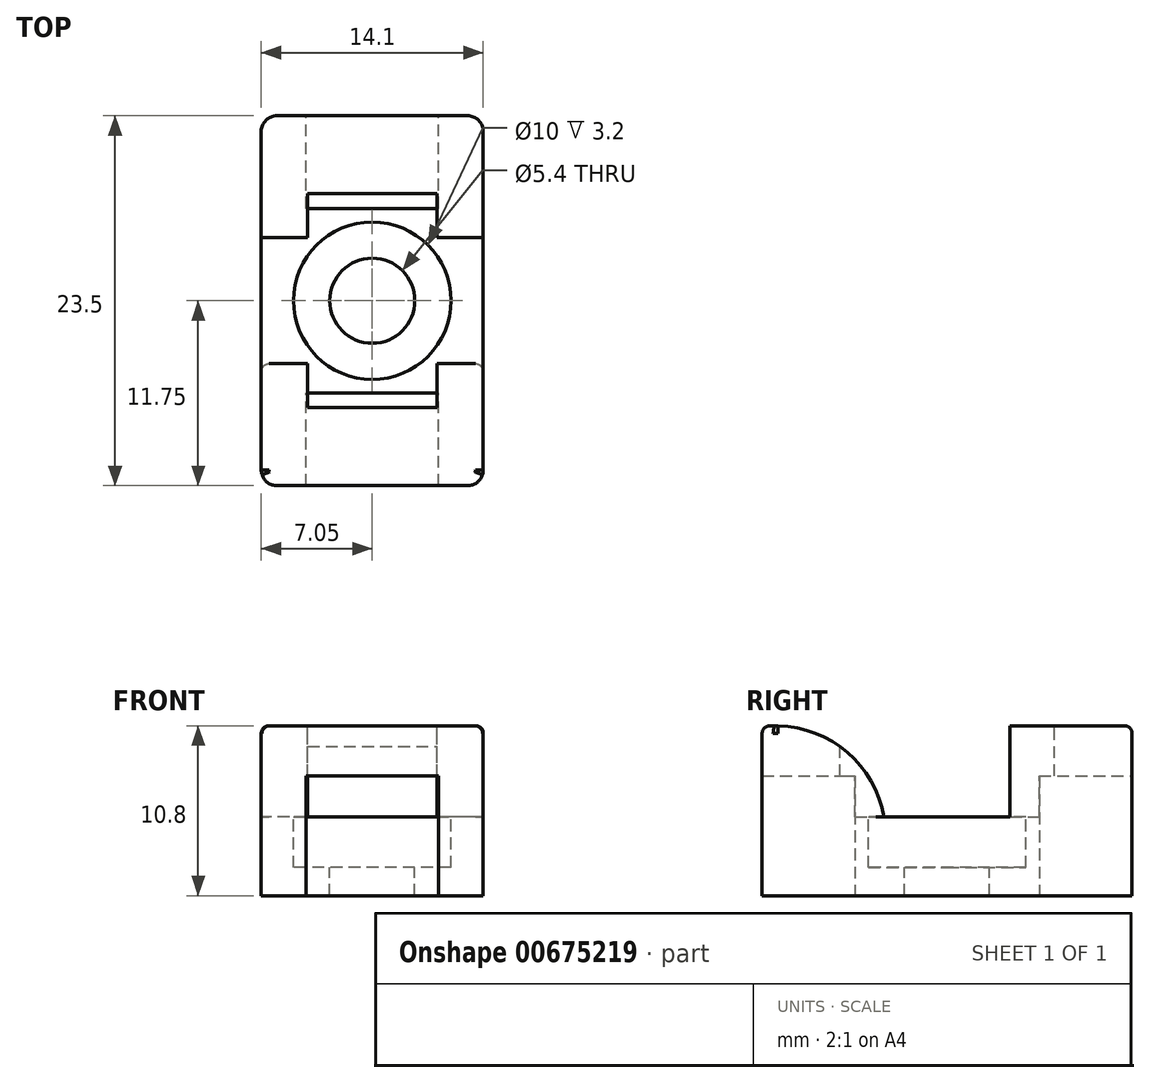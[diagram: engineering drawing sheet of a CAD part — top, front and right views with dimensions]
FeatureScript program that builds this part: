
annotation { "Feature Type Name" : "Feature", "Feature Type Description" : "" }
export const myFeature = defineFeature(function(context is Context, id is Id, definition is map)
    precondition{}
    {
        {
            var Q0;
            Q0=qCreatedBy(makeId("Top.planeOp"),FACE);
            var sketch = newSketch(context, id + "F0", { "sketchPlane" : qUnion([Q0])});
            skLineSegment(sketch, "E0.bottom", {"start": v(7.05, 11.75) * mm, "end": v(-7.05, 11.75) * mm});
            skLineSegment(sketch, "E0.top", {"start": v(7.05, -11.75) * mm, "end": v(-7.05, -11.75) * mm});
            skLineSegment(sketch, "E0.left", {"start": v(7.05, 11.75) * mm, "end": v(7.05, -11.75) * mm});
            skLineSegment(sketch, "E0.right", {"start": v(-7.05, 11.75) * mm, "end": v(-7.05, -11.75) * mm});
            skPoint(sketch, "E0.middle", {"position": v(0, 0) * mm});
            skSolve(sketch);
        }
        {
            var Q0;
            Q0=qSketchRegion(id+"F0",true);
            extrude(context, id + "F1", {"entities" : qUnion([Q0]), "depth" : 10.8 * mm, "offsetDistance" : 25 * mm});
        }
        {
            var Q0;
            Q0=makeQuery(id+"F1.opExtrude","CAP_FACE",FACE,{"disambiguationData":[OSD([sQuery(id+"F0.wireOp",EDGE,"E0.bottom"),sQuery(id+"F0.wireOp",EDGE,"E0.top"),sQuery(id+"F0.wireOp",EDGE,"E0.left"),sQuery(id+"F0.wireOp",EDGE,"E0.right")])],"isStart":false});
            var sketch = newSketch(context, id + "F2", { "sketchPlane" : qUnion([Q0])});
            skLineSegment(sketch, "E1.bottom", {"start": v(4.1, -6.8) * mm, "end": v(-4.1, -6.8) * mm});
            skLineSegment(sketch, "E1.top", {"start": v(4.1, 6.8) * mm, "end": v(-4.1, 6.8) * mm});
            skLineSegment(sketch, "E1.left", {"start": v(4.1, -6.8) * mm, "end": v(4.1, 6.8) * mm});
            skLineSegment(sketch, "E1.right", {"start": v(-4.1, -6.8) * mm, "end": v(-4.1, 6.8) * mm});
            skPoint(sketch, "E1.middle", {"position": v(0, 0) * mm});
            skLineSegment(sketch, "E2.bottom", {"start": v(7.05, -4) * mm, "end": v(-7.05, -4) * mm});
            skLineSegment(sketch, "E2.top", {"start": v(7.05, 4) * mm, "end": v(-7.05, 4) * mm});
            skLineSegment(sketch, "E2.left", {"start": v(7.05, -4) * mm, "end": v(7.05, 4) * mm});
            skLineSegment(sketch, "E2.right", {"start": v(-7.05, -4) * mm, "end": v(-7.05, 4) * mm});
            skSolve(sketch);
        }
        {
            var Q0;
            Q0=qSketchRegion(id+"F2",true);
            extrude(context, id + "F3", {"entities" : qUnion([Q0]), "operationType" : NewBodyOperationType.REMOVE, "oppositeDirection" : true, "depth" : 5.8 * mm, "offsetDistance" : 25 * mm});
        }
        {
            var Q0;
            Q0=makeQuery(id+"F1.opExtrude","CAP_FACE",FACE,{"disambiguationData":[OSD([sQuery(id+"F0.wireOp",EDGE,"E0.bottom"),sQuery(id+"F0.wireOp",EDGE,"E0.top"),sQuery(id+"F0.wireOp",EDGE,"E0.left"),sQuery(id+"F0.wireOp",EDGE,"E0.right")])],"isStart":true});
            var sketch = newSketch(context, id + "F4", { "sketchPlane" : qUnion([Q0])});
            skLineSegment(sketch, "E3.bottom", {"start": v(-4.2, -5.85) * mm, "end": v(4.2, -5.85) * mm});
            skLineSegment(sketch, "E3.top", {"start": v(-4.2, -11.75) * mm, "end": v(4.2, -11.75) * mm});
            skLineSegment(sketch, "E3.left", {"start": v(-4.2, -5.85) * mm, "end": v(-4.2, -11.75) * mm});
            skLineSegment(sketch, "E3.right", {"start": v(4.2, -5.85) * mm, "end": v(4.2, -11.75) * mm});
            skPoint(sketch, "E3.middle", {"position": v(0, -8.8) * mm});
            skLineSegment(sketch, "E4.bottom", {"start": v(-4.2, 11.75) * mm, "end": v(4.2, 11.75) * mm});
            skLineSegment(sketch, "E4.top", {"start": v(-4.2, 5.85) * mm, "end": v(4.2, 5.85) * mm});
            skLineSegment(sketch, "E4.left", {"start": v(-4.2, 11.75) * mm, "end": v(-4.2, 5.85) * mm});
            skLineSegment(sketch, "E4.right", {"start": v(4.2, 11.75) * mm, "end": v(4.2, 5.85) * mm});
            skPoint(sketch, "E4.middle", {"position": v(0, 8.8) * mm});
            skSolve(sketch);
        }
        {
            var Q0;
            Q0=qSketchRegion(id+"F4",true);
            extrude(context, id + "F5", {"entities" : qUnion([Q0]), "operationType" : NewBodyOperationType.REMOVE, "oppositeDirection" : true, "depth" : 7.6 * mm, "offsetDistance" : 25 * mm});
        }
        {
            var Q0;
            Q0=makeQuery(id+"F3.boolean.opBoolean","COPY",FACE,{"derivedFrom":makeQuery(id+"F3.opExtrude","CAP_FACE",FACE,{"disambiguationData":[OSD([sQuery(id+"F2.wireOp",EDGE,"E1.bottom"),sQuery(id+"F2.wireOp",EDGE,"E1.top"),sQuery(id+"F2.wireOp",EDGE,"E1.left"),sQuery(id+"F2.wireOp",EDGE,"E1.right"),sQuery(id+"F2.wireOp",EDGE,"E2.bottom"),sQuery(id+"F2.wireOp",EDGE,"E2.top"),sQuery(id+"F2.wireOp",EDGE,"E2.left"),sQuery(id+"F2.wireOp",EDGE,"E2.right")])],"isStart":false})});
            var sketch = newSketch(context, id + "F6", { "sketchPlane" : qUnion([Q0])});
            skCircle(sketch, "E5", {"center": v(0, 0) * mm, "radius": 5 * mm});
            skSolve(sketch);
        }
        {
            var Q0;
            Q0=qSketchRegion(id+"F6",true);
            extrude(context, id + "F7", {"entities" : qUnion([Q0]), "operationType" : NewBodyOperationType.REMOVE, "oppositeDirection" : true, "depth" : 3.2 * mm, "offsetDistance" : 25 * mm});
        }
        {
            var Q0;
            Q0=makeQuery(id+"F7.boolean.opBoolean","COPY",FACE,{"derivedFrom":makeQuery(id+"F7.opExtrude","CAP_FACE",FACE,{"disambiguationData":[OSD([sQuery(id+"F6.wireOp",EDGE,"E5")])],"isStart":false})});
            var sketch = newSketch(context, id + "F8", { "sketchPlane" : qUnion([Q0])});
            skCircle(sketch, "E6", {"center": v(0, 0) * mm, "radius": 2.7 * mm});
            skSolve(sketch);
        }
        {
            var Q0;
            Q0=qSketchRegion(id+"F8",true);
            extrude(context, id + "F9", {"entities" : qUnion([Q0]), "operationType" : NewBodyOperationType.REMOVE, "endBound" : BoundingType.THROUGH_ALL, "oppositeDirection" : true, "depth" : 25 * mm, "offsetDistance" : 25 * mm});
        }
        {
            var Q0;
            {var subQ0=sQuery(id+"F2.wireOp",EDGE,"E2.bottom");Q0=makeQuery(id+"F3.boolean.opBoolean","COPY",EDGE,{"derivedFrom":makeQuery(id+"F3.opExtrude","CAP_EDGE",EDGE,{"disambiguationData":[OSD([subQ0]),TDD([makeQuery(id+"F2.imprint","IMPRINT",EDGE,{"disambiguationData":[TD([[makeQuery(id+"F2.imprint","INTERSECT",VERTEX,{"derivedFrom":[sQuery(id+"F2.wireOp",EDGE,"E1.right"),subQ0]}),-1.0]])],"derivedFrom":subQ0})])],"isStart":true})});}
            var Q1;
            {var subQ0=sQuery(id+"F2.wireOp",EDGE,"E2.top");Q1=makeQuery(id+"F3.boolean.opBoolean","COPY",EDGE,{"derivedFrom":makeQuery(id+"F3.opExtrude","CAP_EDGE",EDGE,{"disambiguationData":[OSD([subQ0]),TDD([makeQuery(id+"F2.imprint","IMPRINT",EDGE,{"disambiguationData":[TD([[makeQuery(id+"F2.imprint","INTERSECT",VERTEX,{"derivedFrom":[sQuery(id+"F2.wireOp",EDGE,"E1.right"),subQ0]}),-1.0]])],"derivedFrom":subQ0})])],"isStart":true})});}
            fillet(context, id + "F10", {"entities" : qUnion([Q0, Q1]), "radius" : 7 * mm, "tangentPropagation" : true, "allowEdgeOverflow" : false});
        }
        {
            var Q0;
            Q0=makeQuery(id+"F1.opExtrude","SWEPT_EDGE",EDGE,{"disambiguationData":[OSD([sQuery(id+"F0.wireOp",EDGE,"E0.top"),sQuery(id+"F0.wireOp",EDGE,"E0.left")])]});
            var Q1;
            Q1=makeQuery(id+"F1.opExtrude","SWEPT_EDGE",EDGE,{"disambiguationData":[OSD([sQuery(id+"F0.wireOp",EDGE,"E0.top"),sQuery(id+"F0.wireOp",EDGE,"E0.right")])]});
            var Q2;
            Q2=makeQuery(id+"F1.opExtrude","SWEPT_EDGE",EDGE,{"disambiguationData":[OSD([sQuery(id+"F0.wireOp",EDGE,"E0.bottom"),sQuery(id+"F0.wireOp",EDGE,"E0.left")])]});
            var Q3;
            Q3=makeQuery(id+"F1.opExtrude","SWEPT_EDGE",EDGE,{"disambiguationData":[OSD([sQuery(id+"F0.wireOp",EDGE,"E0.bottom"),sQuery(id+"F0.wireOp",EDGE,"E0.right")])]});
            fillet(context, id + "F11", {"entities" : qUnion([Q0, Q1, Q2, Q3]), "radius" : 1 * mm, "tangentPropagation" : true, "allowEdgeOverflow" : false});
        }
        {
            var Q0;
            Q0=makeQuery(id+"F1.opExtrude","CAP_EDGE",EDGE,{"disambiguationData":[OSD([sQuery(id+"F0.wireOp",EDGE,"E0.bottom")])],"isStart":false});
            var Q1;
            Q1=makeQuery(id+"F1.opExtrude","CAP_EDGE",EDGE,{"disambiguationData":[OSD([sQuery(id+"F0.wireOp",EDGE,"E0.top")])],"isStart":false});
            var Q2;
            Q2=makeQuery(id+"F3.boolean.opBoolean","COPY",EDGE,{"derivedFrom":makeQuery(id+"F3.opExtrude","CAP_EDGE",EDGE,{"disambiguationData":[OSD([sQuery(id+"F2.wireOp",EDGE,"E2.right")])],"isStart":false})});
            var Q3;
            Q3=makeQuery(id+"F3.boolean.opBoolean","COPY",EDGE,{"derivedFrom":makeQuery(id+"F3.opExtrude","CAP_EDGE",EDGE,{"disambiguationData":[OSD([sQuery(id+"F2.wireOp",EDGE,"E2.left")])],"isStart":false})});
            fillet(context, id + "F12", {"entities" : qUnion([Q0, Q1, Q2, Q3]), "radius" : .5 * mm, "tangentPropagation" : true, "allowEdgeOverflow" : false});
        }
    });
